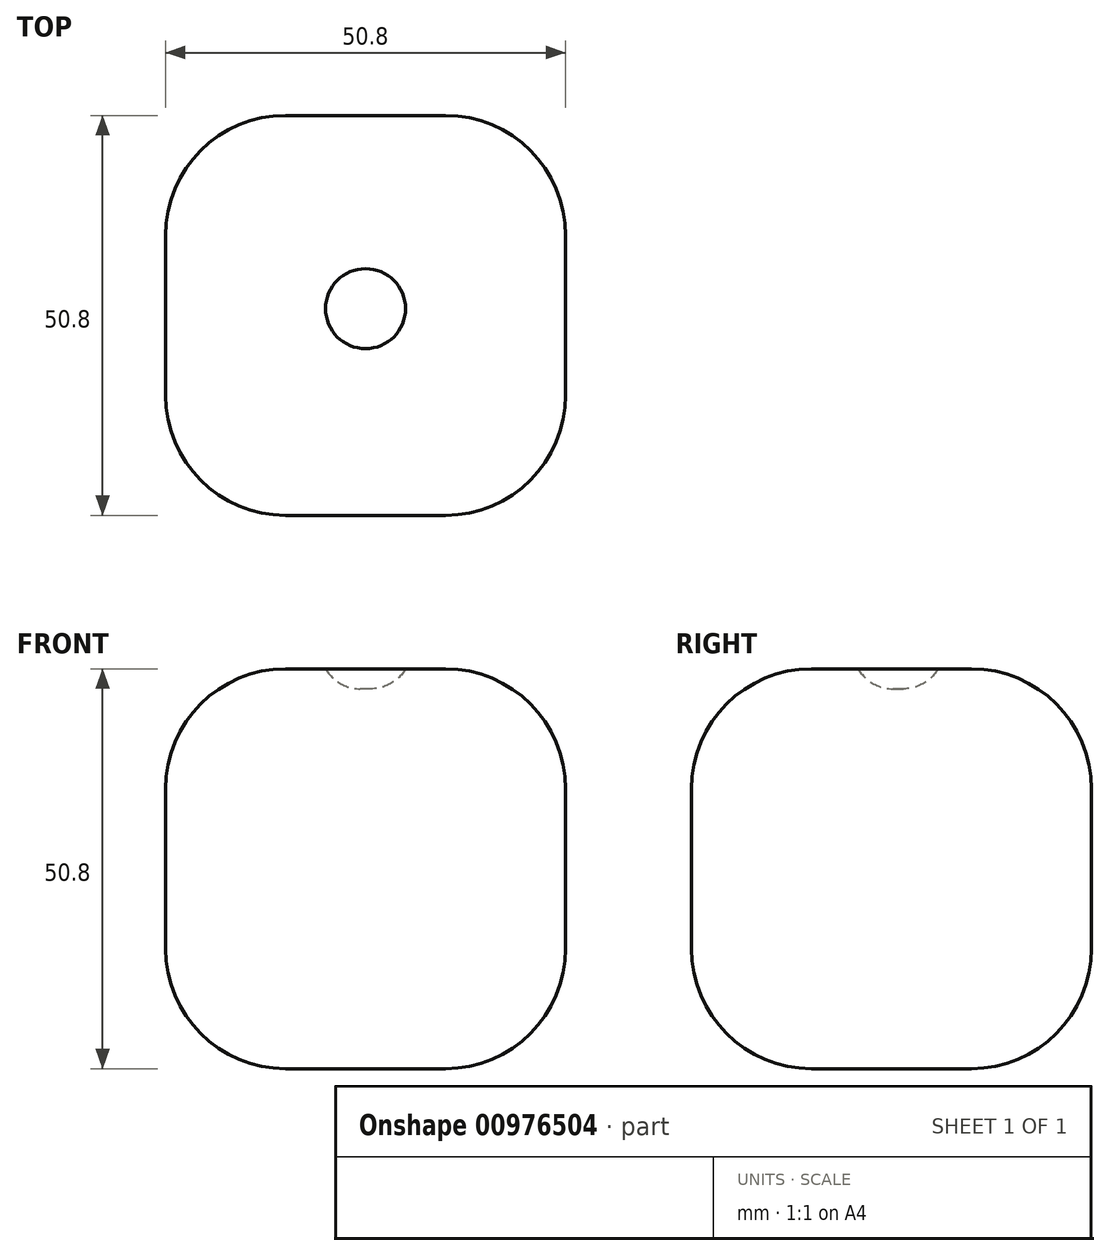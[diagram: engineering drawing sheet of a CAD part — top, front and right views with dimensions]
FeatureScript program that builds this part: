
annotation { "Feature Type Name" : "Feature", "Feature Type Description" : "" }
export const myFeature = defineFeature(function(context is Context, id is Id, definition is map)
    precondition{}
    {
        {
            var Q0;
            Q0=qCreatedBy(makeId("Top.planeOp"),FACE);
            var sketch = newSketch(context, id + "F0", { "sketchPlane" : qUnion([Q0])});
            skLineSegment(sketch, "E0.bottom", {"start": v(0, 0) * mm, "end": v(50.8, 0) * mm});
            skLineSegment(sketch, "E0.top", {"start": v(0, 50.8) * mm, "end": v(50.8, 50.8) * mm});
            skLineSegment(sketch, "E0.left", {"start": v(0, 0) * mm, "end": v(0, 50.8) * mm});
            skLineSegment(sketch, "E0.right", {"start": v(50.8, 0) * mm, "end": v(50.8, 50.8) * mm});
            skSolve(sketch);
        }
        {
            var Q0;
            Q0 = qSketchRegion(id + "F0", true);
            extrude(context, id + "F1", {"entities" : qUnion([Q0]), "depth" : 50.8 * mm, "offsetDistance" : 25.4 * mm});
        }
        {
            var Q0;
            Q0=makeQuery(id+"F1.opExtrude","CAP_EDGE",EDGE,{"disambiguationData":[OSD([sQuery(id+"F0.wireOp",EDGE,"E0.right")])],"isStart":false});
            var Q1;
            Q1=makeQuery(id+"F1.opExtrude","CAP_EDGE",EDGE,{"disambiguationData":[OSD([sQuery(id+"F0.wireOp",EDGE,"E0.bottom")])],"isStart":false});
            var Q2;
            Q2=makeQuery(id+"F1.opExtrude","SWEPT_EDGE",EDGE,{"disambiguationData":[OSD([sQuery(id+"F0.wireOp",EDGE,"E0.bottom"),sQuery(id+"F0.wireOp",EDGE,"E0.right")])]});
            var Q3;
            Q3=makeQuery(id+"F1.opExtrude","SWEPT_EDGE",EDGE,{"disambiguationData":[OSD([sQuery(id+"F0.wireOp",EDGE,"E0.top"),sQuery(id+"F0.wireOp",EDGE,"E0.right")])]});
            var Q4;
            Q4=makeQuery(id+"F1.opExtrude","CAP_EDGE",EDGE,{"disambiguationData":[OSD([sQuery(id+"F0.wireOp",EDGE,"E0.right")])],"isStart":true});
            var Q5;
            Q5=makeQuery(id+"F1.opExtrude","CAP_EDGE",EDGE,{"disambiguationData":[OSD([sQuery(id+"F0.wireOp",EDGE,"E0.bottom")])],"isStart":true});
            var Q6;
            Q6=makeQuery(id+"F1.opExtrude","SWEPT_EDGE",EDGE,{"disambiguationData":[OSD([sQuery(id+"F0.wireOp",EDGE,"E0.bottom"),sQuery(id+"F0.wireOp",EDGE,"E0.left")])]});
            var Q7;
            Q7=makeQuery(id+"F1.opExtrude","CAP_EDGE",EDGE,{"disambiguationData":[OSD([sQuery(id+"F0.wireOp",EDGE,"E0.left")])],"isStart":false});
            var Q8;
            Q8=makeQuery(id+"F1.opExtrude","CAP_EDGE",EDGE,{"disambiguationData":[OSD([sQuery(id+"F0.wireOp",EDGE,"E0.top")])],"isStart":false});
            var Q9;
            Q9=makeQuery(id+"F1.opExtrude","CAP_EDGE",EDGE,{"disambiguationData":[OSD([sQuery(id+"F0.wireOp",EDGE,"E0.top")])],"isStart":true});
            var Q10;
            Q10=makeQuery(id+"F1.opExtrude","CAP_EDGE",EDGE,{"disambiguationData":[OSD([sQuery(id+"F0.wireOp",EDGE,"E0.left")])],"isStart":true});
            var Q11;
            Q11=makeQuery(id+"F1.opExtrude","SWEPT_EDGE",EDGE,{"disambiguationData":[OSD([sQuery(id+"F0.wireOp",EDGE,"E0.top"),sQuery(id+"F0.wireOp",EDGE,"E0.left")])]});
            fillet(context, id + "F2", {"entities" : qUnion([Q0, Q1, Q2, Q3, Q4, Q5, Q6, Q7, Q8, Q9, Q10, Q11]), "radius" : 15.24 * mm, "tangentPropagation" : true, "allowEdgeOverflow" : false});
        }
        {
            var Q0;
            Q0=makeQuery(id+"F1.opExtrude","CAP_FACE",FACE,{"disambiguationData":[OSD([sQuery(id+"F0.wireOp",EDGE,"E0.bottom"),sQuery(id+"F0.wireOp",EDGE,"E0.top"),sQuery(id+"F0.wireOp",EDGE,"E0.left"),sQuery(id+"F0.wireOp",EDGE,"E0.right")])],"isStart":false});
            var sketch = newSketch(context, id + "F3", { "sketchPlane" : qUnion([Q0])});
            skCircle(sketch, "E1", {"center": v(25.4, 26.25) * mm, "radius": 5.08 * mm});
            skPoint(sketch, "E1.centerSnap0", {"position": v(25.4, 35.56) * mm});
            skSolve(sketch);
        }
        {
            var Q0;
            Q0 = qSketchRegion(id + "F3", true);
            extrude(context, id + "F4", {"entities" : qUnion([Q0]), "operationType" : NewBodyOperationType.REMOVE, "oppositeDirection" : true, "depth" : 2.54 * mm, "offsetDistance" : 25.4 * mm});
        }
        {
            var Q0;
            Q0=makeQuery(id+"F4.boolean.opBoolean","COPY",EDGE,{"derivedFrom":makeQuery(id+"F4.opExtrude","CAP_EDGE",EDGE,{"disambiguationData":[OSD([sQuery(id+"F3.wireOp",EDGE,"E1")])],"isStart":false})});
            fillet(context, id + "F5", {"entities" : qUnion([Q0]), "radius" : 5.08 * mm, "tangentPropagation" : true, "allowEdgeOverflow" : false});
        }
    });
